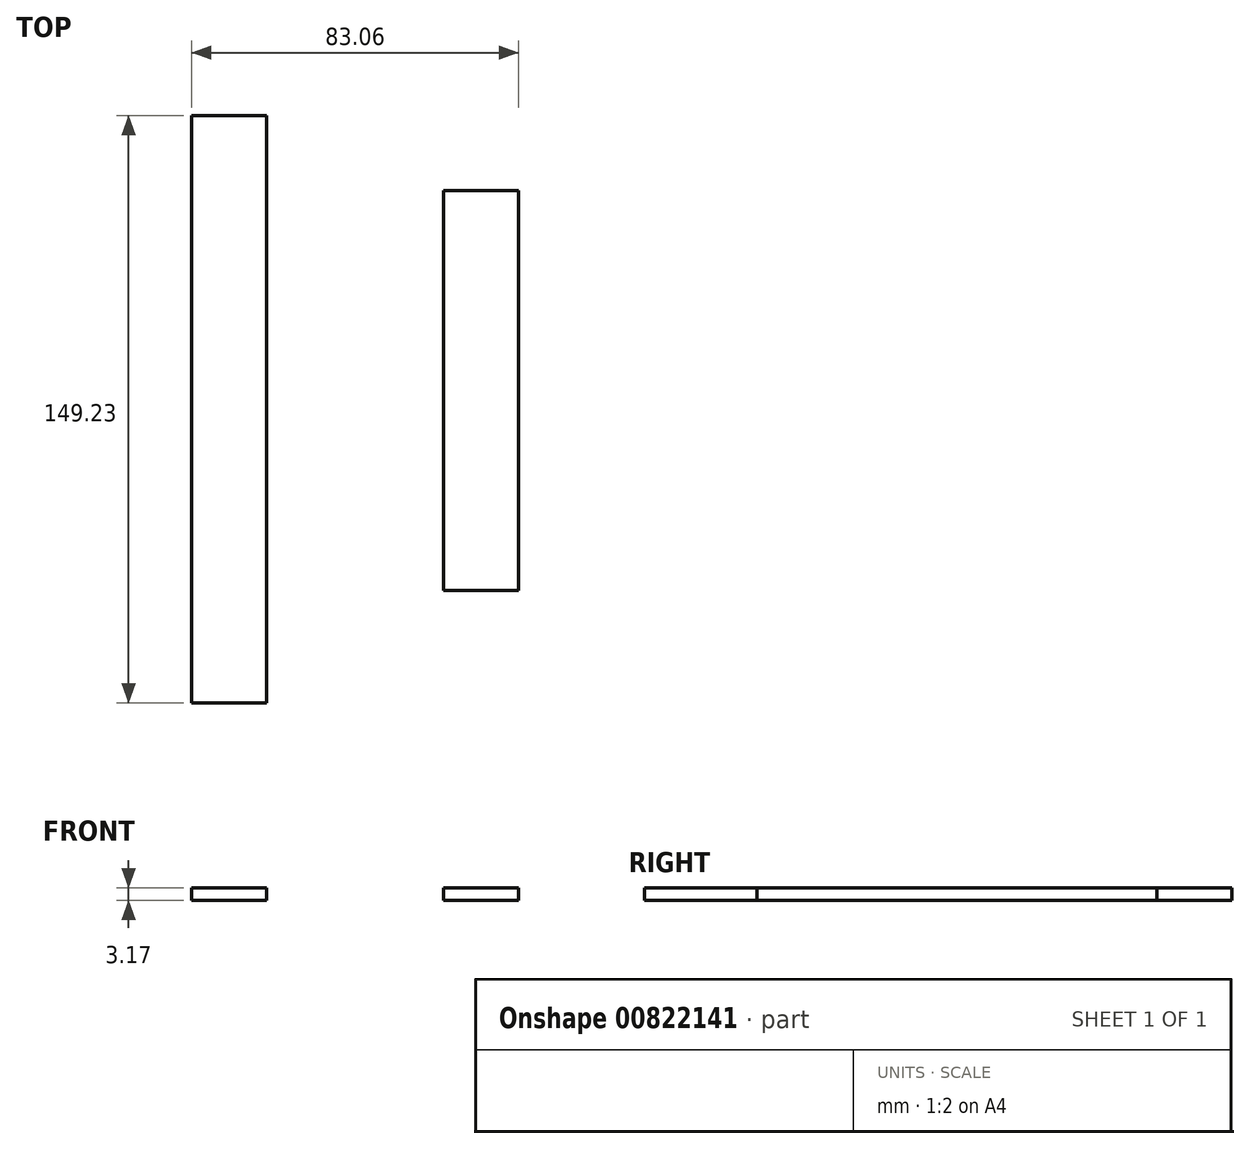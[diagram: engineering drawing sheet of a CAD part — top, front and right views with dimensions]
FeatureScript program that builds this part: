
annotation { "Feature Type Name" : "Feature", "Feature Type Description" : "" }
export const myFeature = defineFeature(function(context is Context, id is Id, definition is map)
    precondition{}
    {
        {
            var Q0;
            Q0=qCreatedBy(makeId("Top.planeOp"),FACE);
            var sketch = newSketch(context, id + "F0", { "sketchPlane" : qUnion([Q0])});
            skLineSegment(sketch, "E0", {"start": v(-38.27, 58.22) * mm, "end": v(-38.27, -91) * mm});
            skLineSegment(sketch, "E1", {"start": v(-38.27, -91) * mm, "end": v(-19.22, -91) * mm});
            skLineSegment(sketch, "E2", {"start": v(-19.22, -91) * mm, "end": v(-19.22, 58.22) * mm});
            skLineSegment(sketch, "E3", {"start": v(-38.27, 58.22) * mm, "end": v(-19.22, 58.22) * mm});
            skLineSegment(sketch, "E4", {"start": v(0, -72.22) * mm, "end": v(3.18, -72.22) * mm});
            skLineSegment(sketch, "E5", {"start": v(3.18, 58.22) * mm, "end": v(0, 58.22) * mm});
            skLineSegment(sketch, "E6", {"start": v(25.74, 39.16) * mm, "end": v(25.74, -62.44) * mm});
            skLineSegment(sketch, "E7", {"start": v(25.74, -62.44) * mm, "end": v(44.79, -62.44) * mm});
            skLineSegment(sketch, "E8", {"start": v(44.79, -62.44) * mm, "end": v(44.79, 39.16) * mm});
            skLineSegment(sketch, "E9", {"start": v(25.74, 39.16) * mm, "end": v(44.79, 39.16) * mm});
            skSolve(sketch);
        }
        {
            var Q0;
            Q0=makeQuery(id+"F0.imprint","IMPRINT",FACE,{"disambiguationData":[TD([[makeQuery(id+"F0.imprint","IMPRINT",EDGE,{"derivedFrom":sQuery(id+"F0.wireOp",EDGE,"E0")}),1.0]])]});
            var Q1;
            Q1=makeQuery(id+"F0.imprint","IMPRINT",FACE,{"disambiguationData":[TD([[makeQuery(id+"F0.imprint","IMPRINT",EDGE,{"derivedFrom":sQuery(id+"F0.wireOp",EDGE,"E6")}),1.0]])]});
            extrude(context, id + "F1", {"entities" : qUnion([Q0, Q1]), "depth" : 3.17 * mm, "offsetDistance" : 25.4 * mm});
        }
    });
